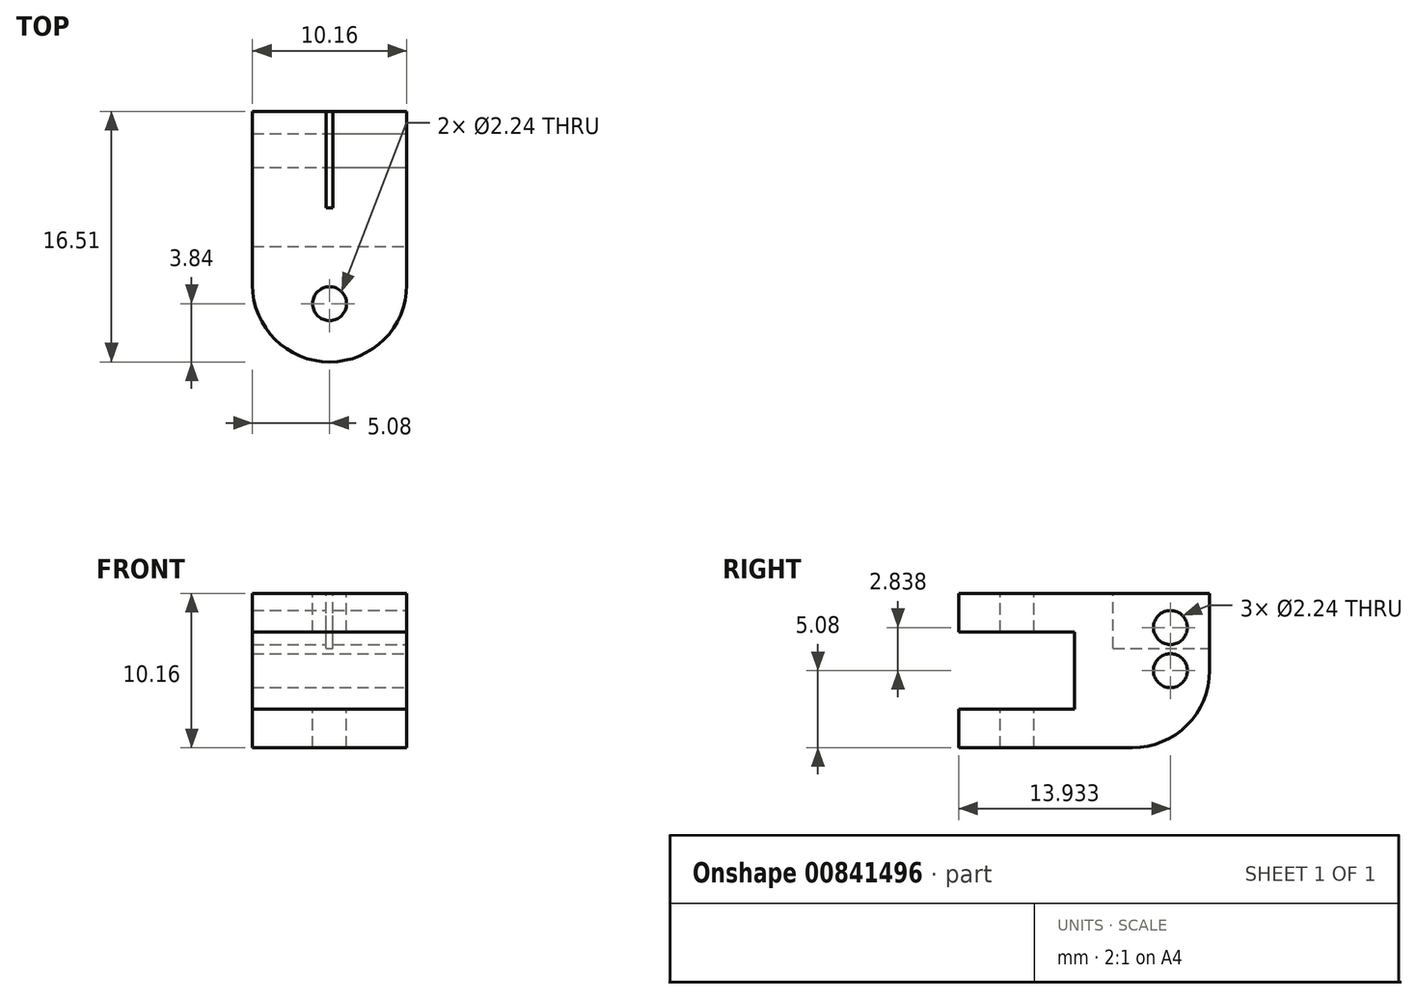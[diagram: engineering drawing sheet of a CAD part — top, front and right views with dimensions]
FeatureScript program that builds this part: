
annotation { "Feature Type Name" : "Feature", "Feature Type Description" : "" }
export const myFeature = defineFeature(function(context is Context, id is Id, definition is map)
    precondition{}
    {
        {
            var Q0;
            Q0=qCreatedBy(makeId("Front.planeOp"),FACE);
            var sketch = newSketch(context, id + "F0", { "sketchPlane" : qUnion([Q0])});
            skLineSegment(sketch, "E0.bottom", {"start": v(-5.08, -5.08) * mm, "end": v(5.08, -5.08) * mm});
            skLineSegment(sketch, "E0.top", {"start": v(-5.08, 5.08) * mm, "end": v(5.08, 5.08) * mm});
            skLineSegment(sketch, "E0.left", {"start": v(-5.08, -5.08) * mm, "end": v(-5.08, 5.08) * mm});
            skLineSegment(sketch, "E0.right", {"start": v(5.08, -5.08) * mm, "end": v(5.08, 5.08) * mm});
            skPoint(sketch, "E0.middle", {"position": v(0, 0) * mm});
            skSolve(sketch);
        }
        {
            var Q0;
            Q0 = qSketchRegion(id + "F0", true);
            extrude(context, id + "F1", {"entities" : qUnion([Q0]), "depth" : 10.16 * mm, "offsetDistance" : 25.4 * mm});
        }
        {
            var Q0;
            Q0=makeQuery(id+"F1.opExtrude","CAP_FACE",FACE,{"disambiguationData":[OSD([sQuery(id+"F0.wireOp",EDGE,"E0.bottom"),sQuery(id+"F0.wireOp",EDGE,"E0.top"),sQuery(id+"F0.wireOp",EDGE,"E0.left"),sQuery(id+"F0.wireOp",EDGE,"E0.right")])],"isStart":false});
            var Q1;
            Q1=makeQuery(id+"F1.opExtrude","SWEPT_FACE",FACE,{"disambiguationData":[OSD([sQuery(id+"F0.wireOp",EDGE,"E0.right")])]});
            var Q2;
            Q2=makeQuery(id+"F1.opExtrude","SWEPT_FACE",FACE,{"disambiguationData":[OSD([sQuery(id+"F0.wireOp",EDGE,"E0.left")])]});
            shell(context, id + "F2", {"entities" : qUnion([Q0, Q1, Q2]), "thickness" : 2.54 * mm});
        }
        {
            var Q0;
            Q0=makeQuery(id+"F1.opExtrude","CAP_FACE",FACE,{"disambiguationData":[OSD([sQuery(id+"F0.wireOp",EDGE,"E0.bottom"),sQuery(id+"F0.wireOp",EDGE,"E0.top"),sQuery(id+"F0.wireOp",EDGE,"E0.left"),sQuery(id+"F0.wireOp",EDGE,"E0.right")])],"isStart":true});
            var sketch = newSketch(context, id + "F3", { "sketchPlane" : qUnion([Q0])});
            skLineSegment(sketch, "E1.bottom", {"start": v(-5.08, 5.08) * mm, "end": v(5.08, 5.08) * mm});
            skLineSegment(sketch, "E1.top", {"start": v(-5.08, -5.08) * mm, "end": v(5.08, -5.08) * mm});
            skLineSegment(sketch, "E1.left", {"start": v(-5.08, 5.08) * mm, "end": v(-5.08, -5.08) * mm});
            skLineSegment(sketch, "E1.right", {"start": v(5.08, 5.08) * mm, "end": v(5.08, -5.08) * mm});
            skSolve(sketch);
        }
        {
            var Q0;
            Q0=makeQuery(id+"F3.imprint","IMPRINT",FACE,{"disambiguationData":[TD([[makeQuery(id+"F3.imprint","IMPRINT",EDGE,{"derivedFrom":sQuery(id+"F3.wireOp",EDGE,"E1.bottom")}),1.0]])]});
            extrude(context, id + "F4", {"entities" : qUnion([Q0]), "operationType" : NewBodyOperationType.ADD, "depth" : 6.35 * mm, "offsetDistance" : 25.4 * mm});
        }
        {
            var Q0;
            Q0=makeQuery(id+"F4.boolean.opBoolean","MERGE",FACE,{"derivedFrom":[makeQuery(id+"F1.opExtrude","SWEPT_FACE",FACE,{"disambiguationData":[OSD([sQuery(id+"F0.wireOp",EDGE,"E0.right")])]}),makeQuery(id+"F4.opExtrude","SWEPT_FACE",FACE,{"disambiguationData":[OSD([sQuery(id+"F3.wireOp",EDGE,"E1.left")])]})]});
            var sketch = newSketch(context, id + "F5", { "sketchPlane" : qUnion([Q0])});
            skCircle(sketch, "E2", {"center": v(3.77, 0) * mm, "radius": 1.12 * mm});
            skCircle(sketch, "E3", {"center": v(3.77, 2.84) * mm, "radius": 1.12 * mm});
            skSolve(sketch);
        }
        {
            var Q0;
            Q0 = qSketchRegion(id + "F5", true);
            extrude(context, id + "F6", {"entities" : qUnion([Q0]), "operationType" : NewBodyOperationType.REMOVE, "oppositeDirection" : true, "depth" : 10.16 * mm, "offsetDistance" : 25.4 * mm});
        }
        {
            var Q0;
            Q0=makeQuery(id+"F4.boolean.opBoolean","MERGE",FACE,{"derivedFrom":[makeQuery(id+"F1.opExtrude","SWEPT_FACE",FACE,{"disambiguationData":[OSD([sQuery(id+"F0.wireOp",EDGE,"E0.top")])]}),makeQuery(id+"F4.opExtrude","SWEPT_FACE",FACE,{"disambiguationData":[OSD([sQuery(id+"F3.wireOp",EDGE,"E1.bottom")])]})]});
            var sketch = newSketch(context, id + "F7", { "sketchPlane" : qUnion([Q0])});
            skCircle(sketch, "E4", {"center": v(0, -6.32) * mm, "radius": 1.12 * mm});
            skSolve(sketch);
        }
        {
            var Q0;
            Q0=makeQuery(id+"F7.imprint","IMPRINT",FACE,{"disambiguationData":[TD([[makeQuery(id+"F7.imprint","IMPRINT",EDGE,{"derivedFrom":sQuery(id+"F7.wireOp",EDGE,"E4")}),1.0]])]});
            var Q1;
            Q1=sQuery(id+"F7.wireOp",EDGE,"E4");
            extrude(context, id + "F8", {"entities" : qUnion([Q0]), "operationType" : NewBodyOperationType.REMOVE, "surfaceEntities" : qUnion([Q1]), "oppositeDirection" : true, "depth" : 10.16 * mm, "offsetDistance" : 25.4 * mm});
        }
        {
            var Q0;
            {var subQ0=sQuery(id+"F0.wireOp",EDGE,"E0.right");Q0=makeQuery(id+"F2.opShell","OFFSET_EDGE",EDGE,{"disambiguationData":[OSD([subQ0]),TDD([makeQuery(id+"F1.opExtrude","CAP_EDGE",EDGE,{"disambiguationData":[OSD([subQ0])],"isStart":false})])]});}
            var Q1;
            {var subQ0=sQuery(id+"F0.wireOp",EDGE,"E0.left");Q1=makeQuery(id+"F2.opShell","OFFSET_EDGE",EDGE,{"disambiguationData":[OSD([subQ0]),TDD([makeQuery(id+"F1.opExtrude","CAP_EDGE",EDGE,{"disambiguationData":[OSD([subQ0])],"isStart":false})])]});}
            var Q2;
            Q2=makeQuery(id+"F1.opExtrude","CAP_EDGE",EDGE,{"disambiguationData":[OSD([sQuery(id+"F0.wireOp",EDGE,"E0.right")])],"isStart":false});
            var Q3;
            Q3=makeQuery(id+"F1.opExtrude","CAP_EDGE",EDGE,{"disambiguationData":[OSD([sQuery(id+"F0.wireOp",EDGE,"E0.left")])],"isStart":false});
            var Q4;
            Q4=makeQuery(id+"F4.opExtrude","CAP_EDGE",EDGE,{"disambiguationData":[OSD([sQuery(id+"F3.wireOp",EDGE,"E1.top")])],"isStart":false});
            fillet(context, id + "F9", {"entities" : qUnion([Q0, Q1, Q2, Q3, Q4]), "radius" : 5.08 * mm, "tangentPropagation" : true, "allowEdgeOverflow" : false});
        }
        {
            var Q0;
            Q0=makeQuery(id+"F4.boolean.opBoolean","MERGE",FACE,{"derivedFrom":[makeQuery(id+"F1.opExtrude","SWEPT_FACE",FACE,{"disambiguationData":[OSD([sQuery(id+"F0.wireOp",EDGE,"E0.top")])]}),makeQuery(id+"F4.opExtrude","SWEPT_FACE",FACE,{"disambiguationData":[OSD([sQuery(id+"F3.wireOp",EDGE,"E1.bottom")])]})]});
            var sketch = newSketch(context, id + "F10", { "sketchPlane" : qUnion([Q0])});
            skLineSegment(sketch, "E5.bottom", {"start": v(0.23, 0) * mm, "end": v(-0.23, 0) * mm});
            skLineSegment(sketch, "E5.top", {"start": v(0.23, 6.35) * mm, "end": v(-0.23, 6.35) * mm});
            skLineSegment(sketch, "E5.left", {"start": v(0.23, 0) * mm, "end": v(0.23, 6.35) * mm});
            skLineSegment(sketch, "E5.right", {"start": v(-0.23, 0) * mm, "end": v(-0.23, 6.35) * mm});
            skSolve(sketch);
        }
        {
            var Q0;
            Q0 = qSketchRegion(id + "F10", true);
            extrude(context, id + "F11", {"entities" : qUnion([Q0]), "operationType" : NewBodyOperationType.REMOVE, "oppositeDirection" : true, "depth" : 3.6 * mm, "offsetDistance" : 25.4 * mm});
        }
    });
